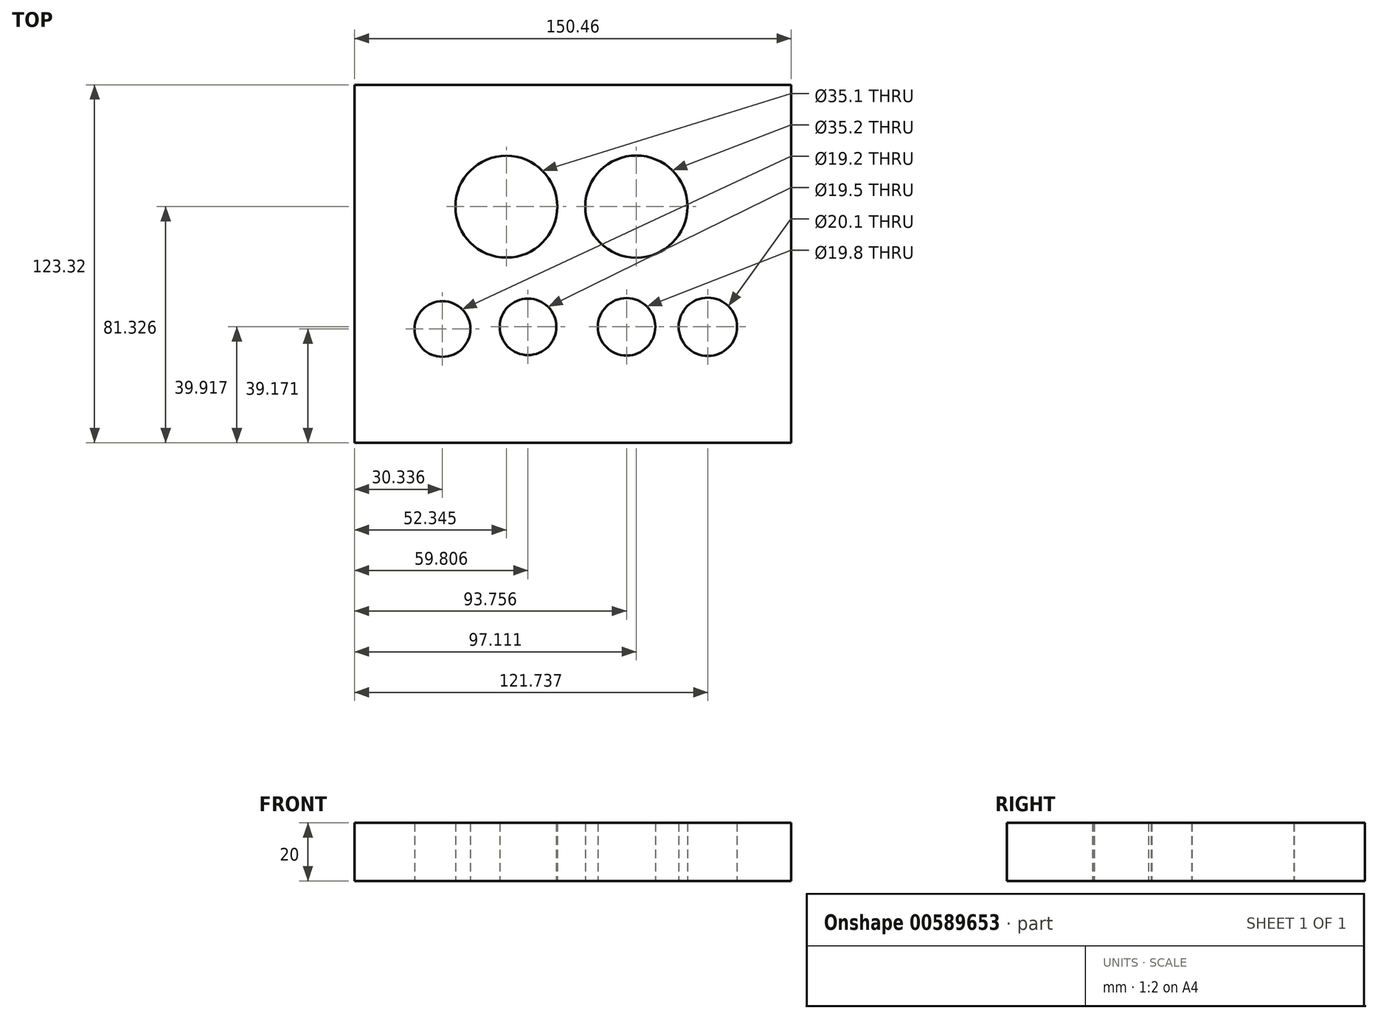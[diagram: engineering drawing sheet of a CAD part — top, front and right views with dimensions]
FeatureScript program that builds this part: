
annotation { "Feature Type Name" : "Feature", "Feature Type Description" : "" }
export const myFeature = defineFeature(function(context is Context, id is Id, definition is map)
    precondition{}
    {
        {
            var Q0;
            Q0=qCreatedBy(makeId("Top.planeOp"),FACE);
            var sketch = newSketch(context, id + "F0", { "sketchPlane" : qUnion([Q0])});
            skLineSegment(sketch, "E0.bottom", {"start": v(75.23, -61.66) * mm, "end": v(-75.23, -61.66) * mm});
            skLineSegment(sketch, "E0.top", {"start": v(75.23, 61.66) * mm, "end": v(-75.23, 61.66) * mm});
            skLineSegment(sketch, "E0.left", {"start": v(75.23, -61.66) * mm, "end": v(75.23, 61.66) * mm});
            skLineSegment(sketch, "E0.right", {"start": v(-75.23, -61.66) * mm, "end": v(-75.23, 61.66) * mm});
            skPoint(sketch, "E0.middle", {"position": v(0, 0) * mm});
            skCircle(sketch, "E1", {"center": v(-22.88, 19.67) * mm, "radius": 17.55 * mm});
            skCircle(sketch, "E2", {"center": v(21.88, 19.67) * mm, "radius": 17.6 * mm});
            skCircle(sketch, "E3", {"center": v(-44.9, -22.49) * mm, "radius": 9.6 * mm});
            skCircle(sketch, "E4", {"center": v(-15.42, -21.74) * mm, "radius": 9.75 * mm});
            skCircle(sketch, "E5", {"center": v(46.5, -21.74) * mm, "radius": 10.05 * mm});
            skCircle(sketch, "E6", {"center": v(18.53, -21.74) * mm, "radius": 9.9 * mm});
            skSolve(sketch);
        }
        {
            var Q0;
            Q0 = qSketchRegion(id + "F0", true);
            extrude(context, id + "F1", {"entities" : qUnion([Q0]), "depth" : 20 * mm, "offsetDistance" : 25 * mm});
        }
    });
